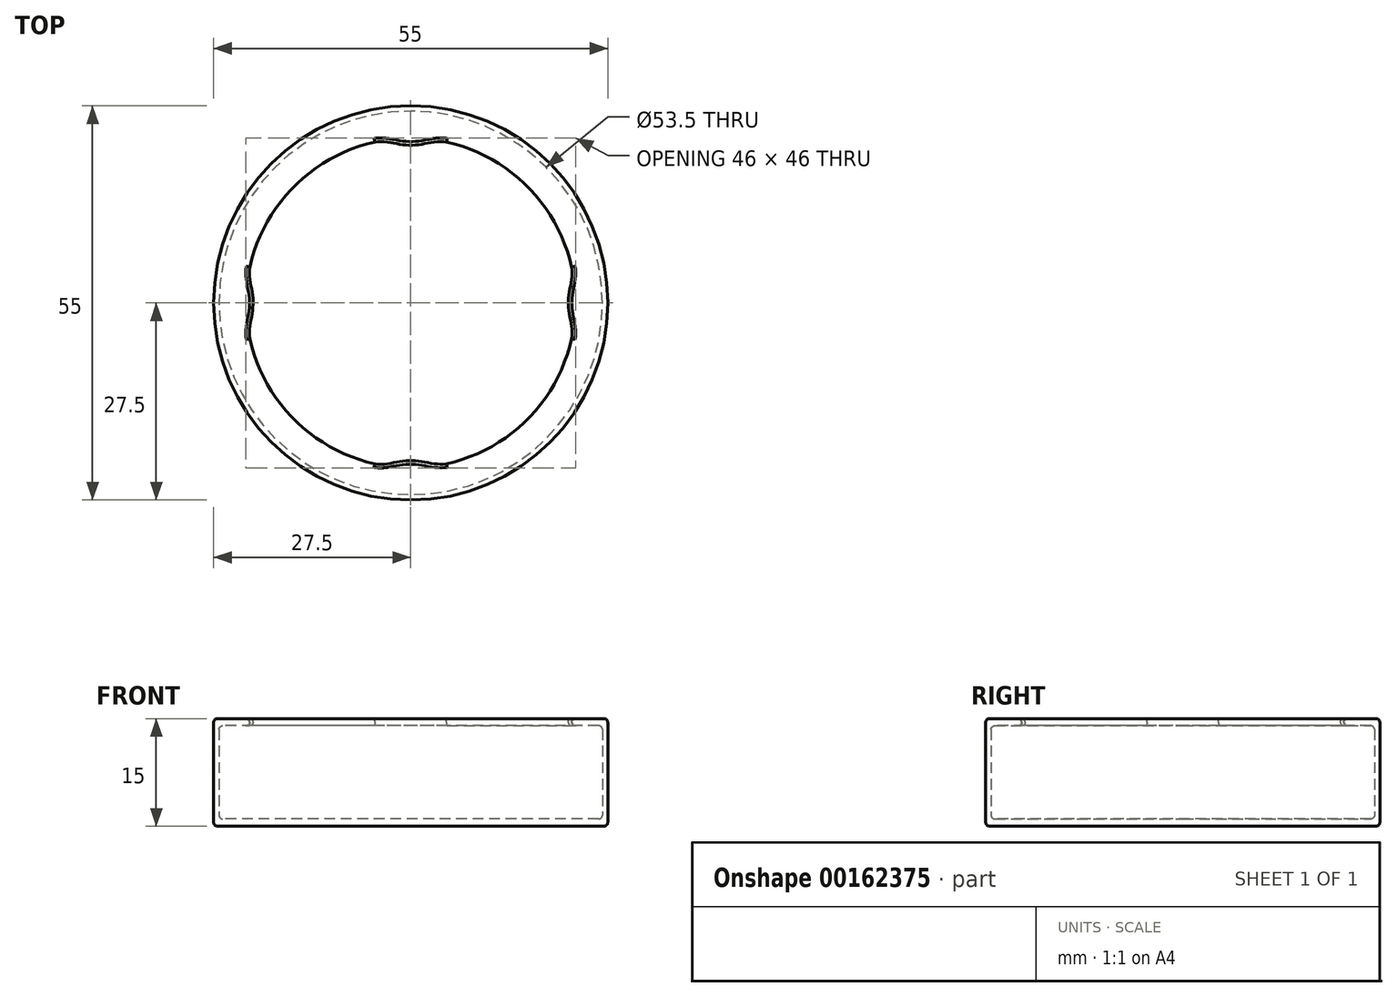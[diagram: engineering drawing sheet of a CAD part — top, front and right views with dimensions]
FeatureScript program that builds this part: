
annotation { "Feature Type Name" : "Feature", "Feature Type Description" : "" }
export const myFeature = defineFeature(function(context is Context, id is Id, definition is map)
    precondition{}
    {
        {
            var Q0;
            Q0=qCreatedBy(makeId("Top.planeOp"),FACE);
            var sketch = newSketch(context, id + "F0", { "sketchPlane" : qUnion([Q0])});
            skCircle(sketch, "E0", {"center": v(0, 0) * mm, "radius": 27.5 * mm});
            skCircle(sketch, "E1", {"center": v(0, 0) * mm, "radius": 26.75 * mm});
            skCircle(sketch, "E2", {"center": v(0, 0) * mm, "radius": 23 * mm});
            skFitSpline(sketch, "E3", {"points": [v(-5, 22.45) * mm, v(0, 22) * mm, v(5, 22.45) * mm], "startDerivative": vector(9, 1.7) * mm, "endDerivative": vector(9, -1.7) * mm});
            skFitSpline(sketch, "E4", {"points": [v(-22.45, 5) * mm, v(-22, 0) * mm, v(-22.45, -5) * mm], "startDerivative": vector(-1.7, -9) * mm, "endDerivative": vector(1.7, -9) * mm});
            skFitSpline(sketch, "E5", {"points": [v(22.45, 5) * mm, v(22, 0) * mm, v(22.45, -5) * mm], "startDerivative": vector(1.7, -9) * mm, "endDerivative": vector(-1.7, -9) * mm});
            skFitSpline(sketch, "E6", {"points": [v(-5, -22.45) * mm, v(0, -22) * mm, v(5, -22.45) * mm], "startDerivative": vector(9, -1.7) * mm, "endDerivative": vector(9, 1.7) * mm});
            skCircle(sketch, "E7", {"center": v(0, 0) * mm, "radius": 22 * mm, "construction": true});
            skSolve(sketch);
        }
        {
            var Q0;
            {var subQ4=sQuery(id+"F0.wireOp",EDGE,"E3");Q0=makeQuery(id+"F0.imprint","IMPRINT",FACE,{"disambiguationData":[TD([[makeQuery(id+"F0.imprint","IMPRINT",EDGE,{"derivedFrom":subQ4}),-1.0]])]});}
            var Q1;
            Q1=makeQuery(id+"F0.imprint","IMPRINT",FACE,{"disambiguationData":[TD([[makeQuery(id+"F0.imprint","IMPRINT",EDGE,{"derivedFrom":sQuery(id+"F0.wireOp",EDGE,"E1")}),1.0]])]});
            var Q2;
            Q2=makeQuery(id+"F0.imprint","IMPRINT",FACE,{"disambiguationData":[TD([[makeQuery(id+"F0.imprint","IMPRINT",EDGE,{"derivedFrom":sQuery(id+"F0.wireOp",EDGE,"E0")}),1.0]])]});
            var Q3;
            {var subQ0=sQuery(id+"F0.wireOp",EDGE,"E4");Q3=makeQuery(id+"F0.imprint","IMPRINT",FACE,{"disambiguationData":[TD([[makeQuery(id+"F0.imprint","IMPRINT",EDGE,{"derivedFrom":subQ0}),-1.0]])]});}
            var Q4;
            {var subQ0=sQuery(id+"F0.wireOp",EDGE,"E6");Q4=makeQuery(id+"F0.imprint","IMPRINT",FACE,{"disambiguationData":[TD([[makeQuery(id+"F0.imprint","IMPRINT",EDGE,{"derivedFrom":subQ0}),-1.0]])]});}
            var Q5;
            {var subQ0=sQuery(id+"F0.wireOp",EDGE,"E5");Q5=makeQuery(id+"F0.imprint","IMPRINT",FACE,{"disambiguationData":[TD([[makeQuery(id+"F0.imprint","IMPRINT",EDGE,{"derivedFrom":subQ0}),1.0]])]});}
            var Q6;
            {var subQ0=sQuery(id+"F0.wireOp",EDGE,"E3");Q6=makeQuery(id+"F0.imprint","IMPRINT",FACE,{"disambiguationData":[TD([[makeQuery(id+"F0.imprint","IMPRINT",EDGE,{"derivedFrom":subQ0}),1.0]])]});}
            extrude(context, id + "F1", {"entities" : qUnion([Q0, Q1, Q2, Q3, Q4, Q5, Q6]), "depth" : 1 * mm});
        }
        {
            var Q0;
            Q0=makeQuery(id+"F0.imprint","IMPRINT",FACE,{"disambiguationData":[TD([[makeQuery(id+"F0.imprint","IMPRINT",EDGE,{"derivedFrom":sQuery(id+"F0.wireOp",EDGE,"E0")}),1.0]])]});
            extrude(context, id + "F2", {"entities" : qUnion([Q0]), "operationType" : NewBodyOperationType.ADD, "depth" : 15 * mm});
        }
        {
            var Q0;
            Q0=makeQuery(id+"F0.imprint","IMPRINT",FACE,{"disambiguationData":[TD([[makeQuery(id+"F0.imprint","IMPRINT",EDGE,{"derivedFrom":sQuery(id+"F0.wireOp",EDGE,"E1")}),1.0]])]});
            var Q1;
            Q1=makeQuery(id+"F0.imprint","IMPRINT",FACE,{"disambiguationData":[TD([[makeQuery(id+"F0.imprint","IMPRINT",EDGE,{"derivedFrom":sQuery(id+"F0.wireOp",EDGE,"E0")}),1.0]])]});
            var Q2;
            {var subQ0=sQuery(id+"F0.wireOp",EDGE,"E4");Q2=makeQuery(id+"F0.imprint","IMPRINT",FACE,{"disambiguationData":[TD([[makeQuery(id+"F0.imprint","IMPRINT",EDGE,{"derivedFrom":subQ0}),-1.0]])]});}
            var Q3;
            {var subQ0=sQuery(id+"F0.wireOp",EDGE,"E3");Q3=makeQuery(id+"F0.imprint","IMPRINT",FACE,{"disambiguationData":[TD([[makeQuery(id+"F0.imprint","IMPRINT",EDGE,{"derivedFrom":subQ0}),1.0]])]});}
            var Q4;
            {var subQ0=sQuery(id+"F0.wireOp",EDGE,"E5");Q4=makeQuery(id+"F0.imprint","IMPRINT",FACE,{"disambiguationData":[TD([[makeQuery(id+"F0.imprint","IMPRINT",EDGE,{"derivedFrom":subQ0}),1.0]])]});}
            var Q5;
            {var subQ0=sQuery(id+"F0.wireOp",EDGE,"E6");Q5=makeQuery(id+"F0.imprint","IMPRINT",FACE,{"disambiguationData":[TD([[makeQuery(id+"F0.imprint","IMPRINT",EDGE,{"derivedFrom":subQ0}),-1.0]])]});}
            extrude(context, id + "F3", {"entities" : qUnion([Q0, Q1, Q2, Q3, Q4, Q5]), "operationType" : NewBodyOperationType.ADD, "depth" : 15 * mm, "hasSecondDirection" : true, "secondDirectionOppositeDirection" : false, "secondDirectionDepth" : 14 * mm});
        }
        {
            var Q0;
            Q0=makeQuery(id+"F2.boolean.opBoolean","INTERSECT",EDGE,{"derivedFrom":[makeQuery(id+"F1.opExtrude","CAP_FACE",FACE,{"disambiguationData":[OSD([sQuery(id+"F0.wireOp",EDGE,"E0")])],"isStart":false}),makeQuery(id+"F2.opExtrude","SWEPT_FACE",FACE,{"disambiguationData":[OSD([sQuery(id+"F0.wireOp",EDGE,"E1")])]})]});
            var Q1;
            Q1=makeQuery(id+"F1.opExtrude","CAP_EDGE",EDGE,{"disambiguationData":[OSD([sQuery(id+"F0.wireOp",EDGE,"E0")])],"isStart":true});
            var Q2;
            Q2=makeQuery(id+"F2.opExtrude","CAP_EDGE",EDGE,{"disambiguationData":[OSD([sQuery(id+"F0.wireOp",EDGE,"E0")])],"isStart":false});
            var Q3;
            Q3=makeQuery(id+"F3.opExtrude","CAP_EDGE",EDGE,{"disambiguationData":[OSD([sQuery(id+"F0.wireOp",EDGE,"E4")])],"isStart":true});
            var Q4;
            Q4=makeQuery(id+"F3.opExtrude","CAP_EDGE",EDGE,{"disambiguationData":[OSD([sQuery(id+"F0.wireOp",EDGE,"E4")])],"isStart":false});
            var Q5;
            {var subQ0=sQuery(id+"F0.wireOp",EDGE,"E2");Q5=makeQuery(id+"F3.opExtrude","CAP_EDGE",EDGE,{"disambiguationData":[OSD([subQ0]),TDD([makeQuery(id+"F0.imprint","IMPRINT",EDGE,{"disambiguationData":[TD([[makeQuery(id+"F0.imprint","INTERSECT",VERTEX,{"disambiguationData":[OD(1.0)],"derivedFrom":[subQ0,sQuery(id+"F0.wireOp",EDGE,"E4")]}),-1.0]])],"derivedFrom":subQ0})])],"isStart":false});}
            var Q6;
            {var subQ0=sQuery(id+"F0.wireOp",EDGE,"E2");Q6=makeQuery(id+"F3.opExtrude","CAP_EDGE",EDGE,{"disambiguationData":[OSD([subQ0]),TDD([makeQuery(id+"F0.imprint","IMPRINT",EDGE,{"disambiguationData":[TD([[makeQuery(id+"F0.imprint","INTERSECT",VERTEX,{"disambiguationData":[OD(1.0)],"derivedFrom":[subQ0,sQuery(id+"F0.wireOp",EDGE,"E4")]}),-1.0]])],"derivedFrom":subQ0})])],"isStart":true});}
            var Q7;
            {var subQ0=sQuery(id+"F0.wireOp",EDGE,"E2");Q7=makeQuery(id+"F3.opExtrude","CAP_EDGE",EDGE,{"disambiguationData":[OSD([subQ0]),TDD([makeQuery(id+"F0.imprint","IMPRINT",EDGE,{"disambiguationData":[TD([[makeQuery(id+"F0.imprint","INTERSECT",VERTEX,{"disambiguationData":[OD(1.0)],"derivedFrom":[subQ0,sQuery(id+"F0.wireOp",EDGE,"E5")]}),1.0]])],"derivedFrom":subQ0})])],"isStart":false});}
            var Q8;
            Q8=makeQuery(id+"F3.opExtrude","CAP_EDGE",EDGE,{"disambiguationData":[OSD([sQuery(id+"F0.wireOp",EDGE,"E6")])],"isStart":false});
            var Q9;
            Q9=makeQuery(id+"F3.opExtrude","CAP_EDGE",EDGE,{"disambiguationData":[OSD([sQuery(id+"F0.wireOp",EDGE,"E6")])],"isStart":true});
            var Q10;
            {var subQ0=sQuery(id+"F0.wireOp",EDGE,"E2");Q10=makeQuery(id+"F3.opExtrude","CAP_EDGE",EDGE,{"disambiguationData":[OSD([subQ0]),TDD([makeQuery(id+"F0.imprint","IMPRINT",EDGE,{"disambiguationData":[TD([[makeQuery(id+"F0.imprint","INTERSECT",VERTEX,{"disambiguationData":[OD(1.0)],"derivedFrom":[subQ0,sQuery(id+"F0.wireOp",EDGE,"E5")]}),1.0]])],"derivedFrom":subQ0})])],"isStart":true});}
            var Q11;
            Q11=makeQuery(id+"F3.opExtrude","CAP_EDGE",EDGE,{"disambiguationData":[OSD([sQuery(id+"F0.wireOp",EDGE,"E5")])],"isStart":false});
            var Q12;
            Q12=makeQuery(id+"F3.opExtrude","CAP_EDGE",EDGE,{"disambiguationData":[OSD([sQuery(id+"F0.wireOp",EDGE,"E5")])],"isStart":true});
            var Q13;
            {var subQ0=sQuery(id+"F0.wireOp",EDGE,"E2");Q13=makeQuery(id+"F3.opExtrude","CAP_EDGE",EDGE,{"disambiguationData":[OSD([subQ0]),TDD([makeQuery(id+"F0.imprint","IMPRINT",EDGE,{"disambiguationData":[TD([[makeQuery(id+"F0.imprint","INTERSECT",VERTEX,{"disambiguationData":[OD(1.0)],"derivedFrom":[subQ0,sQuery(id+"F0.wireOp",EDGE,"E3")]}),1.0]])],"derivedFrom":subQ0})])],"isStart":false});}
            var Q14;
            {var subQ0=sQuery(id+"F0.wireOp",EDGE,"E2");Q14=makeQuery(id+"F3.opExtrude","CAP_EDGE",EDGE,{"disambiguationData":[OSD([subQ0]),TDD([makeQuery(id+"F0.imprint","IMPRINT",EDGE,{"disambiguationData":[TD([[makeQuery(id+"F0.imprint","INTERSECT",VERTEX,{"disambiguationData":[OD(1.0)],"derivedFrom":[subQ0,sQuery(id+"F0.wireOp",EDGE,"E3")]}),1.0]])],"derivedFrom":subQ0})])],"isStart":true});}
            var Q15;
            Q15=makeQuery(id+"F3.opExtrude","CAP_EDGE",EDGE,{"disambiguationData":[OSD([sQuery(id+"F0.wireOp",EDGE,"E3")])],"isStart":false});
            var Q16;
            Q16=makeQuery(id+"F3.opExtrude","CAP_EDGE",EDGE,{"disambiguationData":[OSD([sQuery(id+"F0.wireOp",EDGE,"E3")])],"isStart":true});
            var Q17;
            {var subQ0=sQuery(id+"F0.wireOp",EDGE,"E2");Q17=makeQuery(id+"F3.opExtrude","CAP_EDGE",EDGE,{"disambiguationData":[OSD([subQ0]),TDD([makeQuery(id+"F0.imprint","IMPRINT",EDGE,{"disambiguationData":[TD([[makeQuery(id+"F0.imprint","INTERSECT",VERTEX,{"disambiguationData":[OD(0.0)],"derivedFrom":[subQ0,sQuery(id+"F0.wireOp",EDGE,"E3")]}),-1.0]])],"derivedFrom":subQ0})])],"isStart":true});}
            var Q18;
            {var subQ0=sQuery(id+"F0.wireOp",EDGE,"E2");Q18=makeQuery(id+"F3.opExtrude","CAP_EDGE",EDGE,{"disambiguationData":[OSD([subQ0]),TDD([makeQuery(id+"F0.imprint","IMPRINT",EDGE,{"disambiguationData":[TD([[makeQuery(id+"F0.imprint","INTERSECT",VERTEX,{"disambiguationData":[OD(0.0)],"derivedFrom":[subQ0,sQuery(id+"F0.wireOp",EDGE,"E3")]}),-1.0]])],"derivedFrom":subQ0})])],"isStart":false});}
            var Q19;
            Q19=makeQuery(id+"F3.boolean.opBoolean","INTERSECT",EDGE,{"derivedFrom":[makeQuery(id+"F2.opExtrude","SWEPT_FACE",FACE,{"disambiguationData":[OSD([sQuery(id+"F0.wireOp",EDGE,"E1")])]}),makeQuery(id+"F3.opExtrude","CAP_FACE",FACE,{"disambiguationData":[OSD([sQuery(id+"F0.wireOp",EDGE,"E0"),sQuery(id+"F0.wireOp",EDGE,"E2"),sQuery(id+"F0.wireOp",EDGE,"E3"),sQuery(id+"F0.wireOp",EDGE,"E4"),sQuery(id+"F0.wireOp",EDGE,"E5"),sQuery(id+"F0.wireOp",EDGE,"E6")])],"isStart":true})]});
            fillet(context, id + "F4", {"entities" : qUnion([Q0, Q1, Q2, Q3, Q4, Q5, Q6, Q7, Q8, Q9, Q10, Q11, Q12, Q13, Q14, Q15, Q16, Q17, Q18, Q19]), "radius" : 0.5 * mm, "tangentPropagation" : true, "allowEdgeOverflow" : false});
        }
    });
